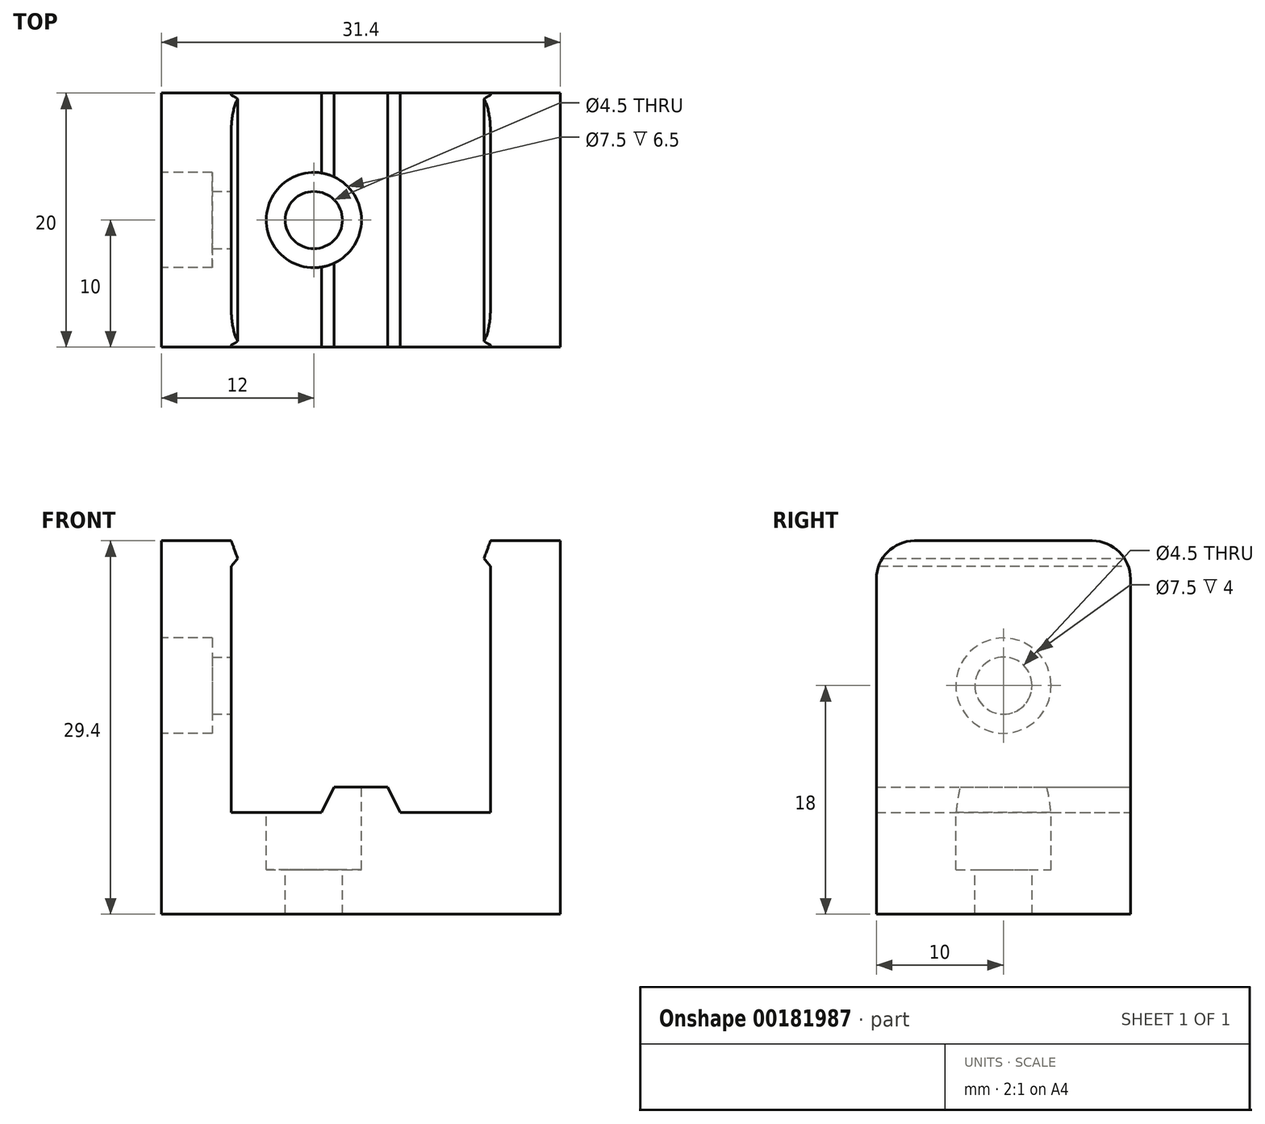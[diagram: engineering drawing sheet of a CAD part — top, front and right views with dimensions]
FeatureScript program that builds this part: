
annotation { "Feature Type Name" : "Feature", "Feature Type Description" : "" }
export const myFeature = defineFeature(function(context is Context, id is Id, definition is map)
    precondition{}
    {
        {
            var Q0;
            Q0=qCreatedBy(makeId("Top.planeOp"),FACE);
            var sketch = newSketch(context, id + "F0", { "sketchPlane" : qUnion([Q0])});
            skLineSegment(sketch, "E0", {"start": v(0, 0) * mm, "end": v(-15.7, 0) * mm});
            skLineSegment(sketch, "E1", {"start": v(-15.7, 0) * mm, "end": v(-15.7, 29.4) * mm});
            skLineSegment(sketch, "E2", {"start": v(-10.2, 29.4) * mm, "end": v(-9.7, 28) * mm});
            skLineSegment(sketch, "E3", {"start": v(-9.7, 28) * mm, "end": v(-10.2, 27.4) * mm});
            skLineSegment(sketch, "E4", {"start": v(-10.2, 27.4) * mm, "end": v(-10.2, 8) * mm});
            skLineSegment(sketch, "E5", {"start": v(-10.2, 8) * mm, "end": v(-3.1, 8) * mm});
            skLineSegment(sketch, "E6", {"start": v(-3.1, 8) * mm, "end": v(-2.1, 10) * mm});
            skLineSegment(sketch, "E7", {"start": v(-2.1, 10) * mm, "end": v(0, 10) * mm});
            skLineSegment(sketch, "E8", {"start": v(-10.2, 29.4) * mm, "end": v(-15.7, 29.4) * mm});
            skLineSegment(sketch, "E9.MirrorCS", {"start": v(2.1, 10) * mm, "end": v(0, 10) * mm});
            skLineSegment(sketch, "E10.MirrorCS", {"start": v(3.1, 8) * mm, "end": v(2.1, 10) * mm});
            skLineSegment(sketch, "E11.MirrorCS", {"start": v(10.2, 8) * mm, "end": v(3.1, 8) * mm});
            skLineSegment(sketch, "E12.MirrorCS", {"start": v(10.2, 27.4) * mm, "end": v(10.2, 8) * mm});
            skLineSegment(sketch, "E13.MirrorCS", {"start": v(9.7, 28) * mm, "end": v(10.2, 27.4) * mm});
            skLineSegment(sketch, "E14.MirrorCS", {"start": v(10.2, 29.4) * mm, "end": v(9.7, 28) * mm});
            skLineSegment(sketch, "E15.MirrorCS", {"start": v(10.2, 29.4) * mm, "end": v(15.7, 29.4) * mm});
            skLineSegment(sketch, "E16.MirrorCS", {"start": v(15.7, 0) * mm, "end": v(15.7, 29.4) * mm});
            skLineSegment(sketch, "E17.MirrorCS", {"start": v(0, 0) * mm, "end": v(15.7, 0) * mm});
            skSolve(sketch);
        }
        {
            var Q0;
            Q0=makeQuery(id+"F0.imprint","IMPRINT",FACE,{"disambiguationData":[TD([[makeQuery(id+"F0.imprint","IMPRINT",EDGE,{"derivedFrom":sQuery(id+"F0.wireOp",EDGE,"E0")}),-1.0]])]});
            extrude(context, id + "F1", {"entities" : qUnion([Q0]), "depth" : 20 * mm});
        }
        {
            var Q0;
            Q0=makeQuery(id+"F1.opExtrude","CAP_EDGE",EDGE,{"disambiguationData":[OSD([sQuery(id+"F0.wireOp",EDGE,"E15.MirrorCS")])],"isStart":false});
            var Q1;
            Q1=makeQuery(id+"F1.opExtrude","CAP_EDGE",EDGE,{"disambiguationData":[OSD([sQuery(id+"F0.wireOp",EDGE,"E8")])],"isStart":false});
            var Q2;
            Q2=makeQuery(id+"F1.opExtrude","CAP_EDGE",EDGE,{"disambiguationData":[OSD([sQuery(id+"F0.wireOp",EDGE,"E8")])],"isStart":true});
            var Q3;
            Q3=makeQuery(id+"F1.opExtrude","CAP_EDGE",EDGE,{"disambiguationData":[OSD([sQuery(id+"F0.wireOp",EDGE,"E15.MirrorCS")])],"isStart":true});
            fillet(context, id + "F2", {"entities" : qUnion([Q0, Q1, Q2, Q3]), "radius" : 3 * mm, "tangentPropagation" : true, "allowEdgeOverflow" : false});
        }
        {
            var Q0;
            Q0=makeQuery(id+"F1.opExtrude","SWEPT_FACE",FACE,{"disambiguationData":[OSD([sQuery(id+"F0.wireOp",EDGE,"E7"),sQuery(id+"F0.wireOp",EDGE,"E9.MirrorCS")])]});
            var sketch = newSketch(context, id + "F3", { "sketchPlane" : qUnion([Q0])});
            skCircle(sketch, "E18", {"center": v(3.7, 10) * mm, "radius": 3.75 * mm});
            skPoint(sketch, "E18.centerSnap0", {"position": v(0, 20) * mm});
            skCircle(sketch, "E19", {"center": v(3.7, 10) * mm, "radius": 2.25 * mm});
            skLineSegment(sketch, "E20", {"start": v(3.7, 0) * mm, "end": v(3.7, 20) * mm, "construction": true});
            skSolve(sketch);
        }
        {
            var Q0;
            {var subQ0=sQuery(id+"F3.wireOp",EDGE,"E19");var subQ1=makeQuery(id+"F1.opExtrude","SWEPT_EDGE",EDGE,{"disambiguationData":[OSD([sQuery(id+"F0.wireOp",EDGE,"E6"),sQuery(id+"F0.wireOp",EDGE,"E7")])]});var subQ2=makeQuery(id+"F3.imprint","INTERSECT",VERTEX,{"disambiguationData":[OD(0.0)],"derivedFrom":[subQ1,subQ0]});Q0=makeQuery(id+"F3.imprint","IMPRINT",FACE,{"disambiguationData":[TD([[makeQuery(id+"F3.imprint","IMPRINT",EDGE,{"disambiguationData":[TD([[subQ2,-1.0]])],"derivedFrom":subQ0}),1.0]])]});}
            var Q1;
            {var subQ0=sQuery(id+"F3.wireOp",EDGE,"E19");var subQ1=makeQuery(id+"F1.opExtrude","SWEPT_EDGE",EDGE,{"disambiguationData":[OSD([sQuery(id+"F0.wireOp",EDGE,"E6"),sQuery(id+"F0.wireOp",EDGE,"E7")])]});var subQ2=makeQuery(id+"F3.imprint","INTERSECT",VERTEX,{"disambiguationData":[OD(0.0)],"derivedFrom":[subQ1,subQ0]});Q1=makeQuery(id+"F3.imprint","IMPRINT",FACE,{"disambiguationData":[TD([[makeQuery(id+"F3.imprint","IMPRINT",EDGE,{"disambiguationData":[TD([[subQ2,1.0]])],"derivedFrom":subQ0}),1.0]])]});}
            extrude(context, id + "F4", {"entities" : qUnion([Q0, Q1]), "operationType" : NewBodyOperationType.REMOVE, "endBound" : BoundingType.THROUGH_ALL, "oppositeDirection" : true, "depth" : 25 * mm});
        }
        {
            var Q0;
            {var subQ0=sQuery(id+"F3.wireOp",EDGE,"E18");var subQ1=makeQuery(id+"F1.opExtrude","SWEPT_EDGE",EDGE,{"disambiguationData":[OSD([sQuery(id+"F0.wireOp",EDGE,"E6"),sQuery(id+"F0.wireOp",EDGE,"E7")])]});var subQ2=makeQuery(id+"F3.imprint","INTERSECT",VERTEX,{"disambiguationData":[OD(0.0)],"derivedFrom":[subQ1,subQ0]});Q0=makeQuery(id+"F3.imprint","IMPRINT",FACE,{"disambiguationData":[TD([[makeQuery(id+"F3.imprint","IMPRINT",EDGE,{"disambiguationData":[TD([[subQ2,-1.0]])],"derivedFrom":subQ0}),1.0]])]});}
            var Q1;
            {var subQ0=sQuery(id+"F3.wireOp",EDGE,"E18");var subQ1=makeQuery(id+"F1.opExtrude","SWEPT_EDGE",EDGE,{"disambiguationData":[OSD([sQuery(id+"F0.wireOp",EDGE,"E6"),sQuery(id+"F0.wireOp",EDGE,"E7")])]});var subQ2=makeQuery(id+"F3.imprint","INTERSECT",VERTEX,{"disambiguationData":[OD(0.0)],"derivedFrom":[subQ1,subQ0]});Q1=makeQuery(id+"F3.imprint","IMPRINT",FACE,{"disambiguationData":[TD([[makeQuery(id+"F3.imprint","IMPRINT",EDGE,{"disambiguationData":[TD([[subQ2,1.0]])],"derivedFrom":subQ0}),1.0]])]});}
            extrude(context, id + "F5", {"entities" : qUnion([Q0, Q1]), "operationType" : NewBodyOperationType.REMOVE, "oppositeDirection" : true, "depth" : 6.5 * mm});
        }
        {
            var Q0;
            Q0=makeQuery(id+"F1.opExtrude","SWEPT_BODY",BODY,{"disambiguationData":[OSD([sQuery(id+"F0.wireOp",EDGE,"E0"),sQuery(id+"F0.wireOp",EDGE,"E1"),sQuery(id+"F0.wireOp",EDGE,"E2"),sQuery(id+"F0.wireOp",EDGE,"E3"),sQuery(id+"F0.wireOp",EDGE,"E4"),sQuery(id+"F0.wireOp",EDGE,"E5"),sQuery(id+"F0.wireOp",EDGE,"E6"),sQuery(id+"F0.wireOp",EDGE,"E7"),sQuery(id+"F0.wireOp",EDGE,"E8"),sQuery(id+"F0.wireOp",EDGE,"E9.MirrorCS"),sQuery(id+"F0.wireOp",EDGE,"E10.MirrorCS"),sQuery(id+"F0.wireOp",EDGE,"E11.MirrorCS"),sQuery(id+"F0.wireOp",EDGE,"E12.MirrorCS"),sQuery(id+"F0.wireOp",EDGE,"E13.MirrorCS"),sQuery(id+"F0.wireOp",EDGE,"E14.MirrorCS"),sQuery(id+"F0.wireOp",EDGE,"E15.MirrorCS"),sQuery(id+"F0.wireOp",EDGE,"E16.MirrorCS"),sQuery(id+"F0.wireOp",EDGE,"E17.MirrorCS")])]});
            var Q1;
            Q1=makeQuery(id+"F1.opExtrude","CAP_EDGE",EDGE,{"disambiguationData":[OSD([sQuery(id+"F0.wireOp",EDGE,"E0"),sQuery(id+"F0.wireOp",EDGE,"E17.MirrorCS")])],"isStart":true});
            transform(context, id + "F6", {"entities" : qUnion([Q0]), "transformType" : TransformType.ROTATION, "transformAxis" : qUnion([Q1]), "angle" : 90 * degree, "oppositeDirection" : true, "makeCopy" : false});
        }
        {
            var Q0;
            Q0=makeQuery(id+"F1.opExtrude","SWEPT_FACE",FACE,{"disambiguationData":[OSD([sQuery(id+"F0.wireOp",EDGE,"E4")])]});
            var sketch = newSketch(context, id + "F7", { "sketchPlane" : qUnion([Q0])});
            skCircle(sketch, "E21", {"center": v(-10, 18) * mm, "radius": 2.25 * mm});
            skLineSegment(sketch, "E22", {"start": v(0, 18) * mm, "end": v(-20, 18) * mm, "construction": true});
            skSolve(sketch);
        }
        {
            var Q0;
            Q0=makeQuery(id+"F7.imprint","IMPRINT",FACE,{"disambiguationData":[TD([[makeQuery(id+"F7.imprint","IMPRINT",EDGE,{"derivedFrom":sQuery(id+"F7.wireOp",EDGE,"E21")}),1.0]])]});
            var Q1;
            Q1=makeQuery(id+"F1.opExtrude","SWEPT_FACE",FACE,{"disambiguationData":[OSD([sQuery(id+"F0.wireOp",EDGE,"E1")])]});
            extrude(context, id + "F8", {"entities" : qUnion([Q0]), "operationType" : NewBodyOperationType.REMOVE, "endBound" : BoundingType.UP_TO_SURFACE, "oppositeDirection" : true, "endBoundEntityFace" : qUnion([Q1]), "depth" : 25 * mm});
        }
        {
            var Q0;
            Q0=makeQuery(id+"F1.opExtrude","SWEPT_FACE",FACE,{"disambiguationData":[OSD([sQuery(id+"F0.wireOp",EDGE,"E1")])]});
            var sketch = newSketch(context, id + "F9", { "sketchPlane" : qUnion([Q0])});
            skCircle(sketch, "E23", {"center": v(10, 18) * mm, "radius": 3.75 * mm});
            skSolve(sketch);
        }
        {
            var Q0;
            Q0=makeQuery(id+"F9.imprint","IMPRINT",FACE,{"disambiguationData":[TD([[makeQuery(id+"F9.imprint","IMPRINT",EDGE,{"derivedFrom":sQuery(id+"F9.wireOp",EDGE,"E23")}),1.0]])]});
            extrude(context, id + "F10", {"entities" : qUnion([Q0]), "operationType" : NewBodyOperationType.REMOVE, "oppositeDirection" : true, "depth" : 4 * mm});
        }
    });
